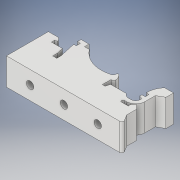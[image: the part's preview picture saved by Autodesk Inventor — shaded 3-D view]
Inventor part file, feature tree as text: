
AUTODESK INVENTOR PART (.ipt)
format: ipt  version: 2019.1 (Build 231200000, 200)  size: 479,232 bytes
history: native  units: in
note: dims shown in document units (in); Inventor stores cm internally (conversion verified against a paired STEP export)
features: extrude x4, sketch x4, thread x3, plane x2, hole x1, fillet x1, move_body x1
ambient origin geometry x8: Origin, YZ Plane, XZ Plane, XY Plane, X Axis, Y Axis, Z Axis, Center Point
bodies: Solid1 (feature_tree), Solid2 (feature_tree)
feature tree (16):
  extrude  "Extrusion1"  Depth=0.8602in
  hole  "Hole1"  [1 undecoded]
  plane  "Work Plane1"
  sketch  "Sketch3"  dims[d4=0.0266in d5=0.1404in d6=45.0deg d7=0.0824in d8=0.0624in]
  extrude  "Extrusion2"  Depth=0.0266in
  thread  "Thread1"  [1 undecoded]
  thread  "Thread2"  [1 undecoded]
  thread  "Thread3"  [1 undecoded]
  extrude  "Extrusion3"  Depth=0.4921in
  fillet  "Fillet1"  Radius=0.0413in
  plane  "Work Plane2"
  extrude  "Extrusion4"  Depth=0.4921in
  move_body  "Move Body1"
  sketch  "Sketch1"  dims[d0=0.8364in d1=0.8602in]
  sketch  "Sketch2"  dims[d2=0.1539in d3=60.0deg]
  sketch  "Sketch5"  dims[d9=0.0339in d10=0.1178in d11=0.0413in d12=0.0514in d13=0.0207in d14=90.0deg d15=0.1339in d16=0.1526in d17=0.1137in d18=150.0deg d19=0.1098in d20=0.1301in d21=0.0707in d22=0.1929in d25=0.0412in d26=1.161in d27=1.8226in d28=0.0533in d29=0.0507in d30=0.0295in d31=0.0543in d32=0.7902in d33=0.0873in d35=0.1052in d36=0.0669in d37=0.0759in d38=0.0433in d39=0.0286in d40=135.0deg d41=0.2283in d44=0.0652in d45=75.0deg d46=0.0392in d47=0.1268in d48=0.012in d49=0.0248in d50=0.0156in d51=0.1076in d52=0.0922in d53=0.0204in d54=0.0052in d55=0.1194in d57=0.0157in d58=0.5374in d59=0.2217in d60=90.0deg d61=0.0472in d62=0.0in d63=0.4331in d64=0.0698in d65=0.065in d66=0.1161in d67=0.0502in d68=0.0456in d69=0.661in d70=0.0591in d71=0.0335in d72=0.0197in d73=0.2228in d74=1.151in d75=0.062in d76=0.0591in d77=0.0721in d78=0.0955in d79=1.151in d80=0.1604in d81=0.0472in d82=0.0325in d83=0.7149in d84=0.0177in d85=0.0529in d86=135.0deg d87=0.2913in d88=0.0787in d89=0.1319in d90=0.0in d91=0.1969in d92=0.1969in d93=0.0in d94=0.0in d95=0.4921in d96=0.4921in d97=0.0in d98=0.0in d99=0.1083in d100=0.2362in d101=0.1575in d102=0.0787in d103=90.0deg d104=0.2894in d105=0.0in d106=0.063in d107=0.1181in d108=0.1181in d109=0.1181in d110=0.2362in d111=0.0in d112=0.3937in d113=0.0in d114=0.3937in d115=0.0in d116=0.3937in d117=0.0in d118=0.2028in d119=0.2028in d120=0.2028in d121=0.0906in d122=0.0in d123=0.0453in d149=0.1535in d150=0.0765in d151=0.0847in d152=0.1096in d153=0.0096in d154=60.0deg d155=4.7244in d157=360.0deg d159=0.0517in d160=0.0in d161=0.4921in d162=0.7874in d164=0.4921in d165=0.7874in d167=0.4921in d170=0.0in d171=0.0in d172=-0.063in]
note: 4 required parameter values undecoded (feature->parameter linkage not recoverable at this tier; creation-order binding heuristic only, values carry confidence <= 0.55)
